# Revit family: PRD_FrankeWS_JntrlSnks_SIRIUSShoe-AndBoot-CleaningUnit_SIRW721A_SIRW721B
name_source: partatom
category: Plumbing Fixtures
revit_build: Autodesk Revit 2018 (Build: 20190510_1515(x64)
units: mm (PartAtom-declared; Revit-internal decimal feet)

## family parameters
Cut with Voids When Loaded = Yes
Host = Face
OmniClass Number = 23.45.05.14.14.27
OmniClass Title = Service Sinks
Part Type = Normal
Room Calculation Point = No
Round Connector Dimension = Use Diameter
Shared = Yes

## types (2) — shared parameters
AssetType = Fixed
BodyMaterial = PRD_AR_ResinBondedMaterial_White
Brushes = Optional
Category = Pr_40_20_96_44, Janitorial sinks
Color = alpine white
Description = Shoe and boot cleaning unit made of MIRANIT resin-bonded mineral material with pore-free smooth surface (temperature-resistant up to 80°C). For wall mounting. Large inner radii, bottom of basin with 2° slope. Alpine white colour. Drain with under-screwed waste unit with DN 100 horizontal outlet including removable sludge bucket made of stainless steel. Waste unit rotatable by 90°. One hinged grating made of stainless steel for each wash place. Welded substructure frame, powder-coated in basin colour, adjustable base feet. Mounting material included.
DiameterNominal = 100  [stored 0.328084 ft]
DrainSize = 100 mm  [stored 0.328084 ft]
DurationUnit = year
Finish = High polished
Grid = Hinged
GrossWeight = 105.00 kg
IfcExportAs = IfcSanitaryTerminalType
IfcExportType = SINK
IntegralAccessories = Mounting material included
Manufacturer = KWC Group AG
ManufacturerName = KWC Group AG
ManufacturerURL = www.kwc.com
Material = Mineral material
MaterialCode = Miranit
Mounting = BackToWall
NBSDescription = Janitorial units
NBSReference = 45-35-70/401
NetWeight = 80.00 kg
NominalDepth = 510 mm  [stored 1.67323 ft]
NominalHeight = 500 mm  [stored 1.64042 ft]
NominalWidth = 1400 mm  [stored 4.59318 ft]
NumberOfWashPlaces = 2
OutletSize = DN 100
ProductInformation = https://pim.kwc.com
SinkType = USERDEFINED
Size = 1400 x 175/500 x 510 mm (W x H x D)
Splashback = No
StandMaterial = PRD_AR_Black
StrainerMaterial = PRD_AR_StainlessSteel_SatinFinished
Sump = Yes
SumpBasket = Included
TailorMade = No
TapLedge = No
TypeOfMounting = Wall mounting
URL = www.kwc.com
Uniclass2015Code = Pr_40_20_96_44
Uniclass2015Title = Janitorial sinks
Uniclass2015Version = Products v1.23
Version = 1
WarrantyDurationUnit = year
WasteHolePosition = Center
zero-valued in all types: Default Elevation, MountingOffset

## per-type parameters (varying)
| type | BIMObjectName | Features | ModelNumber | Name | ProductCode |
| SIRW721A | PRD_AR_JanitorialSinks_SIRIUSShoe-AndBoot-CleaningUnit_SIRW721A | Dimensions 1400 x 175/500 x 510 mm (W x H x D) | 2000102727 | SIRIUS Shoe- and boot-cleaning unit SIRW721A | 207.0638.412 |
| SIRW721B | PRD_AR_JanitorialSinks_SIRIUSShoe-AndBoot-CleaningUnit_SIRW721B | Dimensions 1400 x 175/500 x 510 mm (W x H x D). For customer-provided siphon | 2000102728 | SIRIUS Shoe- and boot-cleaning unit SIRW721B | 207.0638.413 |

note: column(s) folded — value = type name in every type: Model, ModelReference

note: [stored X ft] marks values corroborated as IEEE doubles in the binary element streams (Revit-internal decimal feet)

## geometry (parser evidence)
native form markers: Sweep x4
no freeform markers — native parametric forms only
